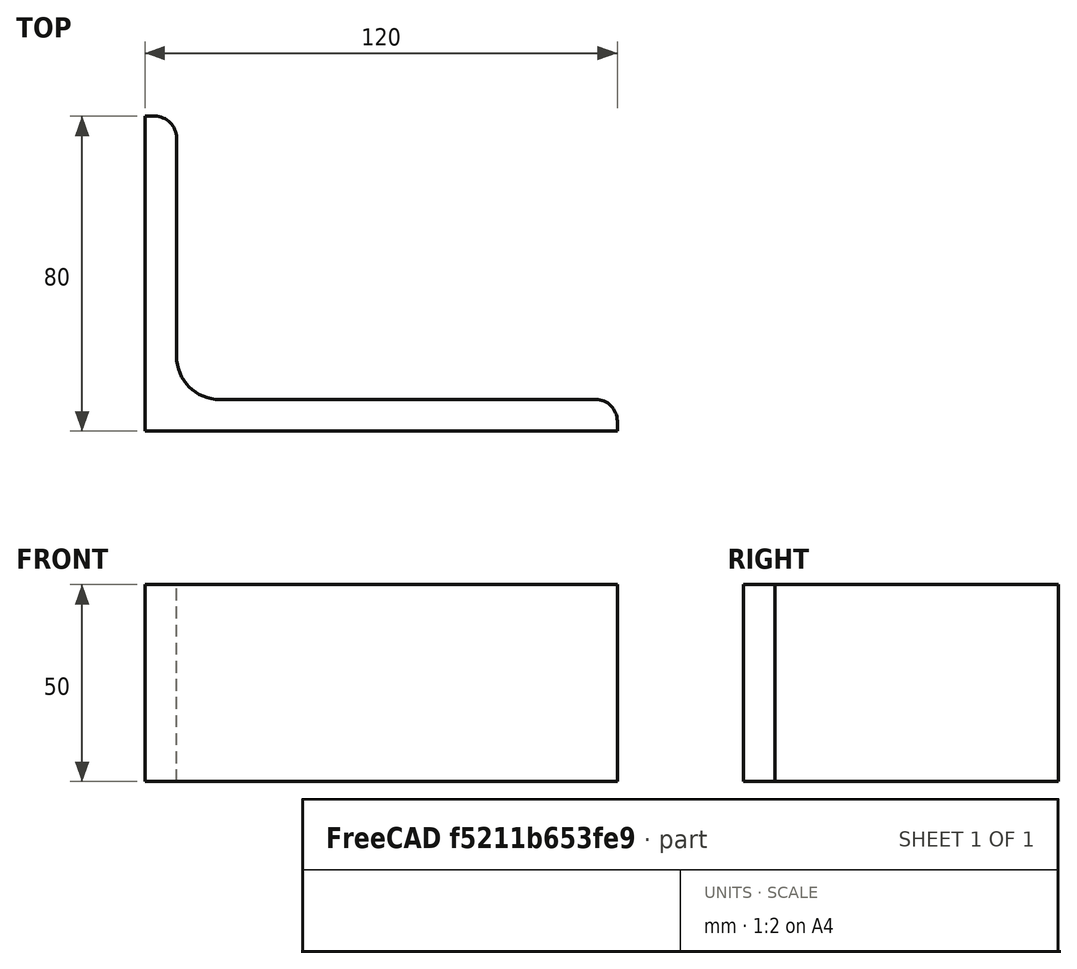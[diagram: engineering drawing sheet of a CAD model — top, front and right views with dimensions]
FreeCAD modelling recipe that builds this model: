
FCSTD DOCUMENT  (FreeCAD 0.15R4671 (Git))
Label: Angle Bar 120x80x8 EN10056 S235JR
License: All rights reserved
LicenseURL: http://en.wikipedia.org/wiki/All_rights_reserved
objects: Sketcher::SketchObject×1, Part::Extrusion×1
note: 2 computed .brp shape members not serialized (recipe doc carries the construction recipe); baked Part::Feature solids carry a one-line shape summary decoded from their .brp

FEATURE [Sketcher::SketchObject] Sketch
  sketch-geometry (9):
    g0: LineSegment StartX=0 StartY=0 StartZ=0 EndX=120 EndY=0 EndZ=0
    g1: LineSegment StartX=120 StartY=0 StartZ=0 EndX=120 EndY=2.5 EndZ=0
    g2: LineSegment StartX=114.5 StartY=8 StartZ=0 EndX=19 EndY=8 EndZ=0
    g3: LineSegment StartX=0 StartY=0 StartZ=0 EndX=0 EndY=80 EndZ=0
    g4: LineSegment StartX=0 StartY=80 StartZ=0 EndX=2.5 EndY=80 EndZ=0
    g5: LineSegment StartX=8 StartY=74.5 StartZ=0 EndX=8 EndY=19 EndZ=0
    g6: ArcOfCircle CenterX=19 CenterY=19 CenterZ=0 NormalX=0 NormalY=0 NormalZ=1 Radius=11 StartAngle=3.14159 EndAngle=4.71239
    g7: ArcOfCircle CenterX=2.5 CenterY=74.5 CenterZ=0 NormalX=0 NormalY=0 NormalZ=1 Radius=5.5 StartAngle=0 EndAngle=1.5708
    g8: ArcOfCircle CenterX=114.5 CenterY=2.5 CenterZ=0 NormalX=0 NormalY=0 NormalZ=1 Radius=5.5 StartAngle=0 EndAngle=1.5708
  constraints (23):
    c: Coincident(g0,g-1)
    c: Horizontal(g0)
    c: Coincident(g1,g0)
    c: Vertical(g1)
    c: Horizontal(g2)
    c: Coincident(g3,g-1)
    c: Vertical(g3)
    c: Coincident(g4,g3)
    c: Horizontal(g4)
    c: Vertical(g5)
    c: Tangent(g5,g6) = -1.5708
    c: Tangent(g2,g6) = 1.5708
    c: Tangent(g4,g7) = 1.5708
    c: Tangent(g5,g7) = 1.5708
    c: Tangent(g2,g8) = -1.5708
    c: Tangent(g1,g8) = -1.5708
    c: DistanceX(g0) = 120
    c: DistanceY(g3) = 80
    c: DistanceY(g0,g2) = 8
    c: DistanceX(g3,g5) = 8
    c: Radius(g6) = 11
    c: Radius(g8) = 5.5
    c: Radius(g7) = 5.5
FEATURE [Part::Extrusion] Extrude  label="Angle Bar 120x80x8 EN10056 S235JR"
  Base = -> Sketch
  Dir = (0,0,50)
  Solid = true
